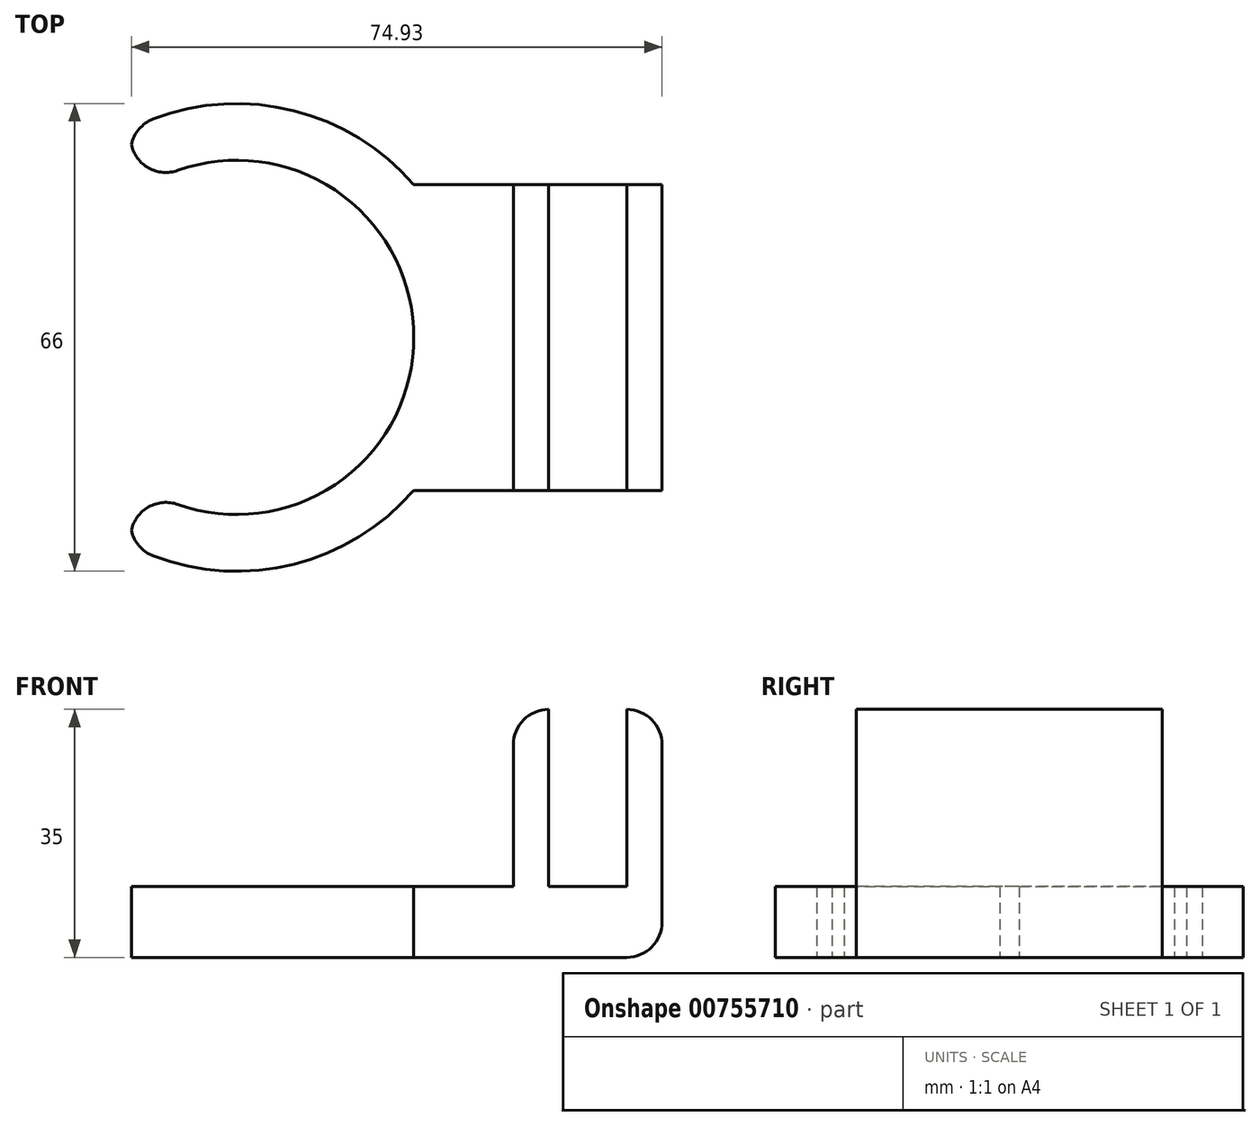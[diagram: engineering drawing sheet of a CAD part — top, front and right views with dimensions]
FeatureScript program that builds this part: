
annotation { "Feature Type Name" : "Feature", "Feature Type Description" : "" }
export const myFeature = defineFeature(function(context is Context, id is Id, definition is map)
    precondition{}
    {
        {
            var Q0;
            Q0=qCreatedBy(makeId("Top.planeOp"),FACE);
            var sketch = newSketch(context, id + "F0", { "sketchPlane" : qUnion([Q0])});
            skArc(sketch, "E0", {"start": v(-47, -20) * mm, "mid": v(-7, 0) * mm, "end": v(-47, 20) * mm});
            skArc(sketch, "E1", {"start": v(-47, -29.4) * mm, "mid": v(1, 0) * mm, "end": v(-47, 29.4) * mm});
            skLineSegment(sketch, "E2", {"start": v(-47, 29.4) * mm, "end": v(-47, 20) * mm});
            skLineSegment(sketch, "E3.trimOffspring", {"start": v(-47, -20) * mm, "end": v(-47, -29.4) * mm});
            skLineSegment(sketch, "E4.bottom", {"start": v(-7.04, 21.58) * mm, "end": v(7.04, 21.58) * mm});
            skLineSegment(sketch, "E4.top", {"start": v(-7.04, -21.58) * mm, "end": v(7.04, -21.58) * mm});
            skLineSegment(sketch, "E4.left", {"start": v(-7.04, 21.58) * mm, "end": v(-7.04, -21.58) * mm});
            skLineSegment(sketch, "E4.right", {"start": v(7.04, 21.58) * mm, "end": v(7.04, -21.58) * mm});
            skPoint(sketch, "E4.middle", {"position": v(0, 0) * mm});
            skLineSegment(sketch, "E5.bottom", {"start": v(7.04, 21.58) * mm, "end": v(12.04, 21.58) * mm});
            skLineSegment(sketch, "E5.top", {"start": v(7.04, -21.58) * mm, "end": v(12.04, -21.58) * mm});
            skLineSegment(sketch, "E5.right", {"start": v(12.04, 21.58) * mm, "end": v(12.04, -21.58) * mm});
            skLineSegment(sketch, "E6.bottom", {"start": v(12.04, 21.58) * mm, "end": v(23.04, 21.58) * mm});
            skLineSegment(sketch, "E6.top", {"start": v(12.04, -21.58) * mm, "end": v(23.04, -21.58) * mm});
            skLineSegment(sketch, "E6.right", {"start": v(23.04, 21.58) * mm, "end": v(23.04, -21.58) * mm});
            skLineSegment(sketch, "E7.bottom", {"start": v(23.04, 21.58) * mm, "end": v(28.04, 21.58) * mm});
            skLineSegment(sketch, "E7.top", {"start": v(23.04, -21.58) * mm, "end": v(28.04, -21.58) * mm});
            skLineSegment(sketch, "E7.right", {"start": v(28.04, 21.58) * mm, "end": v(28.04, -21.58) * mm});
            skSolve(sketch);
        }
        {
            var Q0;
            Q0=qSketchRegion(id+"F0",true);
            var Q1;
            {var subQ0=sQuery(id+"F0.wireOp",EDGE,"45a05517-1ebe-4f36-a2c0-a8144c21bbce1.MirrorCS");var subQ1=sQuery(id+"F0.wireOp",EDGE,"E1");var subQ2=makeQuery(id+"F0.imprint","INTERSECT",VERTEX,{"disambiguationData":[OD(0.0)],"derivedFrom":[subQ1,subQ0]});Q1=makeQuery(id+"F0.imprint","IMPRINT",FACE,{"disambiguationData":[TD([[makeQuery(id+"F0.imprint","IMPRINT",EDGE,{"disambiguationData":[TD([[subQ2,-1.0]])],"derivedFrom":subQ1}),1.0]])]});}
            extrude(context, id + "F1", {"entities" : qUnion([Q0, Q1]), "depth" : 5 * mm, "offsetDistance" : 25 * mm, "hasSecondDirection" : true, "secondDirectionOppositeDirection" : true, "secondDirectionDepth" : 5 * mm});
        }
        {
            var Q0;
            Q0=makeQuery(id+"F1.opExtrude","SWEPT_EDGE",EDGE,{"disambiguationData":[OSD([sQuery(id+"F0.wireOp",EDGE,"E0"),sQuery(id+"F0.wireOp",EDGE,"E2")])]});
            var Q1;
            Q1=makeQuery(id+"F1.opExtrude","SWEPT_EDGE",EDGE,{"disambiguationData":[OSD([sQuery(id+"F0.wireOp",EDGE,"E1"),sQuery(id+"F0.wireOp",EDGE,"E3.trimOffspring")])]});
            var Q2;
            Q2=makeQuery(id+"F1.opExtrude","SWEPT_EDGE",EDGE,{"disambiguationData":[OSD([sQuery(id+"F0.wireOp",EDGE,"E0"),sQuery(id+"F0.wireOp",EDGE,"E3.trimOffspring")])]});
            var Q3;
            Q3=makeQuery(id+"F1.opExtrude","SWEPT_EDGE",EDGE,{"disambiguationData":[OSD([sQuery(id+"F0.wireOp",EDGE,"E1"),sQuery(id+"F0.wireOp",EDGE,"E2")])]});
            var Q4;
            Q4=makeQuery(id+"F1.opExtrude","SWEPT_EDGE",EDGE,{"disambiguationData":[OSD([sQuery(id+"F0.wireOp",EDGE,"45a05517-1ebe-4f36-a2c0-a8144c21bbce1.MirrorCS"),sQuery(id+"F0.wireOp",EDGE,"45a05517-1ebe-4f36-a2c0-a8144c21bbce3.MirrorCS")])]});
            var Q5;
            Q5=makeQuery(id+"F1.opExtrude","SWEPT_EDGE",EDGE,{"disambiguationData":[OSD([sQuery(id+"F0.wireOp",EDGE,"45a05517-1ebe-4f36-a2c0-a8144c21bbce0.MirrorCS"),sQuery(id+"F0.wireOp",EDGE,"45a05517-1ebe-4f36-a2c0-a8144c21bbce3.MirrorCS")])]});
            var Q6;
            Q6=makeQuery(id+"F1.opExtrude","SWEPT_EDGE",EDGE,{"disambiguationData":[OSD([sQuery(id+"F0.wireOp",EDGE,"45a05517-1ebe-4f36-a2c0-a8144c21bbce0.MirrorCS"),sQuery(id+"F0.wireOp",EDGE,"45a05517-1ebe-4f36-a2c0-a8144c21bbce2.MirrorCS")])]});
            var Q7;
            Q7=makeQuery(id+"F1.opExtrude","SWEPT_EDGE",EDGE,{"disambiguationData":[OSD([sQuery(id+"F0.wireOp",EDGE,"45a05517-1ebe-4f36-a2c0-a8144c21bbce1.MirrorCS"),sQuery(id+"F0.wireOp",EDGE,"45a05517-1ebe-4f36-a2c0-a8144c21bbce2.MirrorCS")])]});
            fillet(context, id + "F2", {"entities" : qUnion([Q0, Q1, Q2, Q3, Q4, Q5, Q6, Q7]), "radius" : 5 * mm, "tangentPropagation" : true, "allowEdgeOverflow" : false});
        }
        {
            var Q0;
            Q0=makeQuery(id+"F1.opExtrude","CAP_FACE",FACE,{"disambiguationData":[OSD([sQuery(id+"F0.wireOp",EDGE,"E0"),sQuery(id+"F0.wireOp",EDGE,"E1"),sQuery(id+"F0.wireOp",EDGE,"E2"),sQuery(id+"F0.wireOp",EDGE,"E3.trimOffspring"),sQuery(id+"F0.wireOp",EDGE,"E4.bottom"),sQuery(id+"F0.wireOp",EDGE,"E4.top"),sQuery(id+"F0.wireOp",EDGE,"E4.left"),sQuery(id+"F0.wireOp",EDGE,"E5.bottom"),sQuery(id+"F0.wireOp",EDGE,"E5.top"),sQuery(id+"F0.wireOp",EDGE,"E6.bottom"),sQuery(id+"F0.wireOp",EDGE,"E6.top"),sQuery(id+"F0.wireOp",EDGE,"E7.bottom"),sQuery(id+"F0.wireOp",EDGE,"E7.top"),sQuery(id+"F0.wireOp",EDGE,"E7.right")])],"isStart":false});
            var sketch = newSketch(context, id + "F3", { "sketchPlane" : qUnion([Q0])});
            skLineSegment(sketch, "E8.0", {"start": v(7.04, 21.58) * mm, "end": v(7.04, -21.58) * mm});
            skLineSegment(sketch, "E9.0", {"start": v(12.04, 21.58) * mm, "end": v(12.04, -21.58) * mm});
            skLineSegment(sketch, "E10.0", {"start": v(23.04, 21.58) * mm, "end": v(23.04, -21.58) * mm});
            skLineSegment(sketch, "E11.0", {"start": v(28.04, 21.58) * mm, "end": v(28.04, -21.58) * mm});
            skLineSegment(sketch, "E12.bottom", {"start": v(7.04, 21.58) * mm, "end": v(12.04, 21.58) * mm});
            skLineSegment(sketch, "E12.top", {"start": v(7.04, -21.58) * mm, "end": v(12.04, -21.58) * mm});
            skLineSegment(sketch, "E13.bottom", {"start": v(23.04, 21.58) * mm, "end": v(28.04, 21.58) * mm});
            skLineSegment(sketch, "E13.top", {"start": v(23.04, -21.58) * mm, "end": v(28.04, -21.58) * mm});
            skSolve(sketch);
        }
        {
            var Q0;
            Q0=qSketchRegion(id+"F3",true);
            extrude(context, id + "F4", {"entities" : qUnion([Q0]), "operationType" : NewBodyOperationType.ADD, "depth" : 25 * mm, "offsetDistance" : 25 * mm});
        }
        {
            var Q0;
            Q0=makeQuery(id+"F4.opExtrude","CAP_EDGE",EDGE,{"disambiguationData":[OSD([sQuery(id+"F3.wireOp",EDGE,"E8.0")])],"isStart":true});
            var Q1;
            Q1=makeQuery(id+"F4.opExtrude","CAP_EDGE",EDGE,{"disambiguationData":[OSD([sQuery(id+"F3.wireOp",EDGE,"E8.0")])],"isStart":false});
            var Q2;
            Q2=makeQuery(id+"F4.opExtrude","CAP_EDGE",EDGE,{"disambiguationData":[OSD([sQuery(id+"F3.wireOp",EDGE,"E11.0")])],"isStart":false});
            var Q3;
            Q3=makeQuery(id+"F1.opExtrude","CAP_EDGE",EDGE,{"disambiguationData":[OSD([sQuery(id+"F0.wireOp",EDGE,"E7.right")])],"isStart":true});
            fillet(context, id + "F5", {"entities" : qUnion([Q0, Q1, Q2, Q3]), "radius" : 5 * mm, "tangentPropagation" : true, "allowEdgeOverflow" : false});
        }
    });
